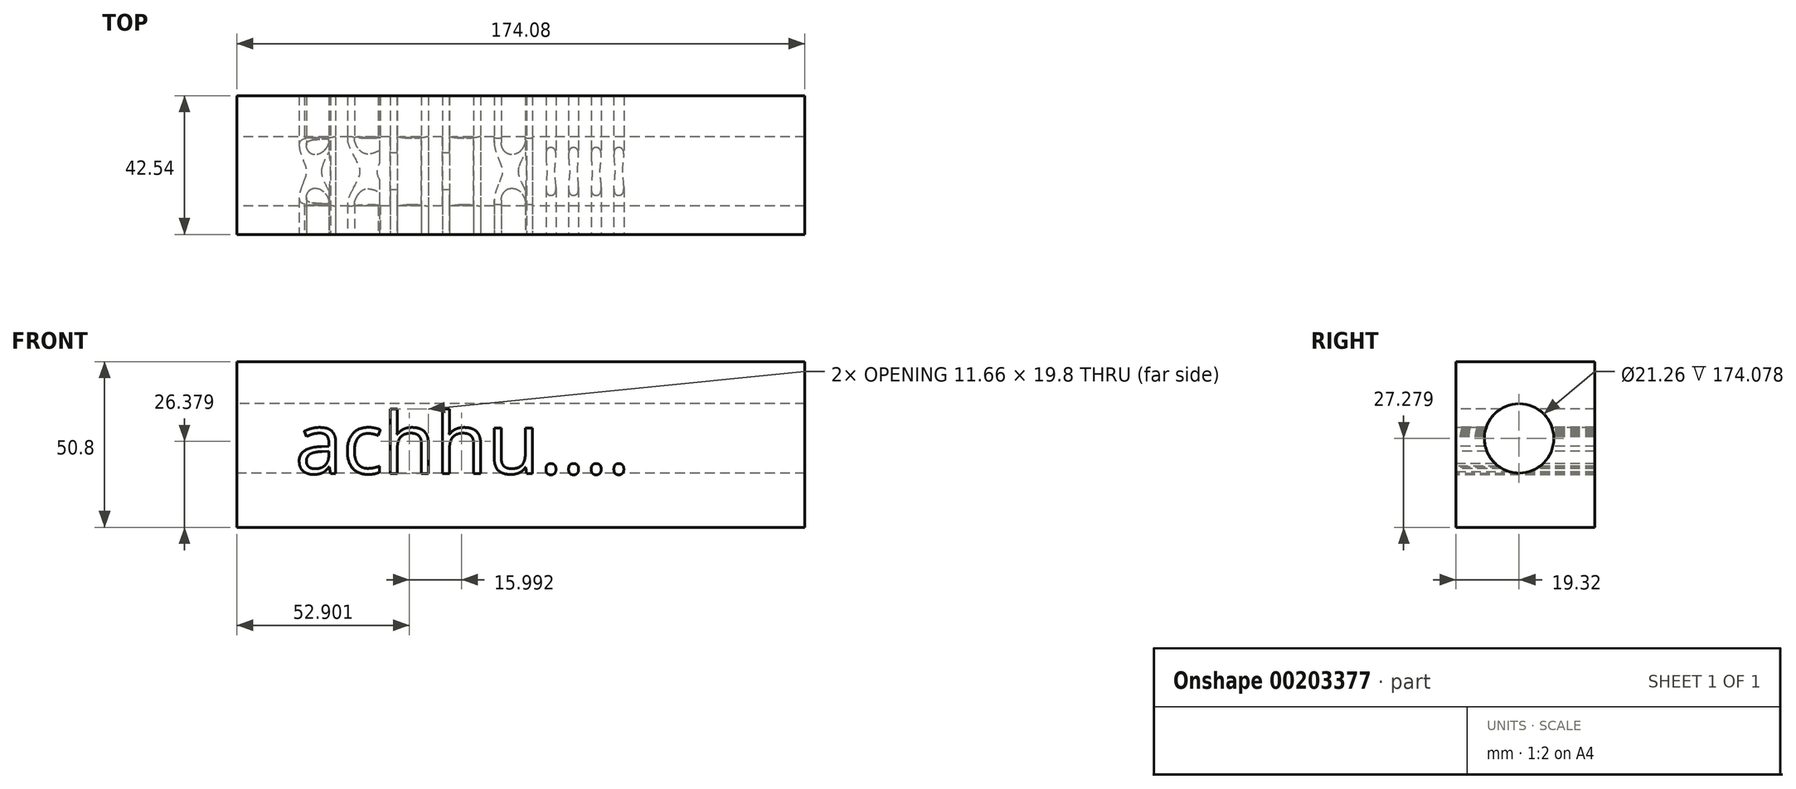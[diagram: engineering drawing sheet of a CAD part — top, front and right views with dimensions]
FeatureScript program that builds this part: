
annotation { "Feature Type Name" : "Feature", "Feature Type Description" : "" }
export const myFeature = defineFeature(function(context is Context, id is Id, definition is map)
    precondition{}
    {
        {
            var Q0;
            Q0=qCreatedBy(makeId("Top.planeOp"),FACE);
            var sketch = newSketch(context, id + "F0", { "sketchPlane" : qUnion([Q0])});
            skLineSegment(sketch, "E0.bottom", {"start": v(-62.95, 23.22) * mm, "end": v(111.13, 23.22) * mm});
            skLineSegment(sketch, "E0.top", {"start": v(-62.95, -19.32) * mm, "end": v(111.13, -19.32) * mm});
            skLineSegment(sketch, "E0.left", {"start": v(-62.95, 23.22) * mm, "end": v(-62.95, -19.32) * mm});
            skLineSegment(sketch, "E0.right", {"start": v(111.13, 23.22) * mm, "end": v(111.13, -19.32) * mm});
            skSolve(sketch);
        }
        {
            var Q0;
            Q0=makeQuery(id+"F0.imprint","IMPRINT",FACE,{"disambiguationData":[TD([[makeQuery(id+"F0.imprint","IMPRINT",EDGE,{"derivedFrom":sQuery(id+"F0.wireOp",EDGE,"E0.bottom")}),-1.0]])]});
            extrude(context, id + "F1", {"entities" : qUnion([Q0]), "depth" : 50.8 * mm});
        }
        {
            var Q0;
            Q0=makeQuery(id+"F1.opExtrude","SWEPT_FACE",FACE,{"disambiguationData":[OSD([sQuery(id+"F0.wireOp",EDGE,"E0.left")])]});
            var sketch = newSketch(context, id + "F2", { "sketchPlane" : qUnion([Q0])});
            skCircle(sketch, "E1", {"center": v(0, 27.28) * mm, "radius": 10.63 * mm});
            skSolve(sketch);
        }
        {
            var Q0;
            Q0=makeQuery(id+"F2.imprint","IMPRINT",FACE,{"disambiguationData":[TD([[makeQuery(id+"F2.imprint","IMPRINT",EDGE,{"derivedFrom":sQuery(id+"F2.wireOp",EDGE,"E1")}),1.0]])]});
            extrude(context, id + "F3", {"entities" : qUnion([Q0]), "operationType" : NewBodyOperationType.REMOVE, "oppositeDirection" : true, "depth" : 177.8 * mm});
        }
        {
            var Q0;
            Q0=makeQuery(id+"F1.opExtrude","SWEPT_FACE",FACE,{"disambiguationData":[OSD([sQuery(id+"F0.wireOp",EDGE,"E0.top")])]});
            var sketch = newSketch(context, id + "F4", { "sketchPlane" : qUnion([Q0])});
            skText(sketch, "E2", { "text": "achhu....", "fontName": "OpenSans-Regular.ttf"});
            const initialGuessF4  = {"E2": [-0.04501, 0.01648, 1, 0, 0.01876]};
            skSetInitialGuess(sketch, initialGuessF4);
            skSolve(sketch);
        }
        {
            var Q0;
            Q0 = qSketchRegion(id + "F4", true);
            extrude(context, id + "F5", {"entities" : qUnion([Q0]), "operationType" : NewBodyOperationType.REMOVE, "oppositeDirection" : true, "depth" : 50.8 * mm});
        }
    });
